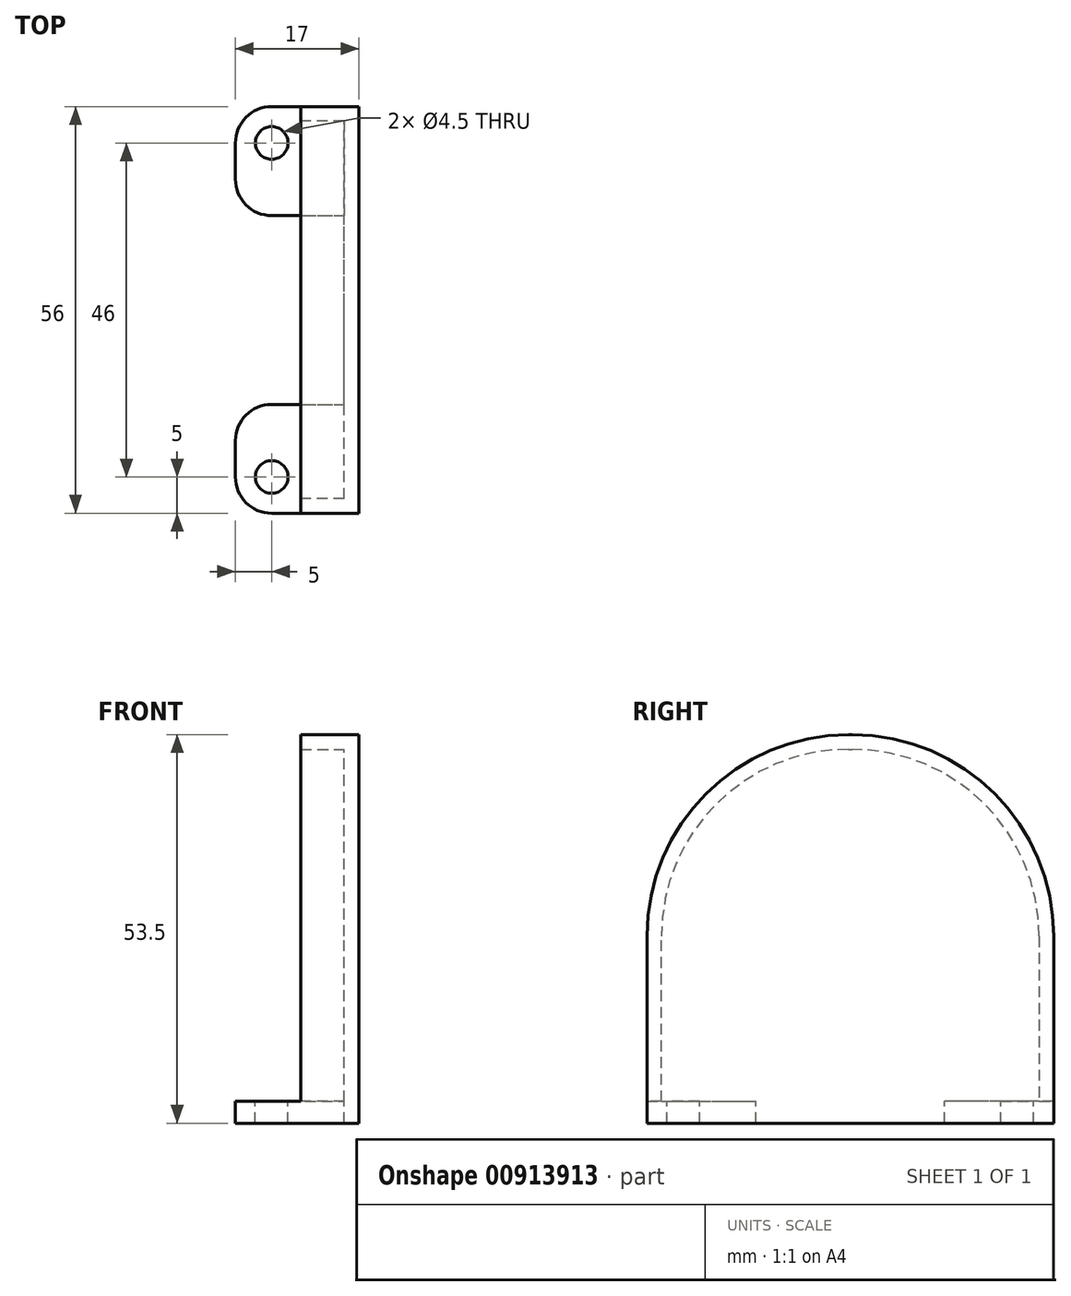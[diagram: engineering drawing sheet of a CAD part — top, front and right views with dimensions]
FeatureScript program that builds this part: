
annotation { "Feature Type Name" : "Feature", "Feature Type Description" : "" }
export const myFeature = defineFeature(function(context is Context, id is Id, definition is map)
    precondition{}
    {
        {
            var Q0;
            Q0=qCreatedBy(makeId("Right.planeOp"),FACE);
            var sketch = newSketch(context, id + "F0", { "sketchPlane" : qUnion([Q0])});
            skLineSegment(sketch, "E0.bottom", {"start": v(-28, 0) * mm, "end": v(28, 0) * mm});
            skLineSegment(sketch, "E0.top", {"start": v(-0.25, 53.5) * mm, "end": v(0.25, 53.5) * mm});
            skLineSegment(sketch, "E0.left", {"start": v(-28, 0) * mm, "end": v(-28, 25.75) * mm});
            skLineSegment(sketch, "E0.right", {"start": v(28, 0) * mm, "end": v(28, 25.75) * mm});
            skPoint(sketch, "E1.visualSharp", {"position": v(-28, 53.5) * mm});
            skArc(sketch, "E1.filletArc", {"start": v(-0.25, 53.5) * mm, "mid": v(-19.87, 45.37) * mm, "end": v(-28, 25.75) * mm});
            skPoint(sketch, "E2.visualSharp", {"position": v(28, 53.5) * mm});
            skArc(sketch, "E2.filletArc", {"start": v(28, 25.75) * mm, "mid": v(19.87, 45.37) * mm, "end": v(0.25, 53.5) * mm});
            skLineSegment(sketch, "E3", {"start": v(-28, 25.75) * mm, "end": v(28, 25.75) * mm, "construction": true});
            skSolve(sketch);
        }
        {
            var Q0;
            Q0=qSketchRegion(id+"F0",true);
            extrude(context, id + "F1", {"entities" : qUnion([Q0]), "depth" : 2 * mm, "offsetDistance" : 25 * mm});
        }
        {
            var Q0;
            Q0=makeQuery(id+"F1.opExtrude","CAP_FACE",FACE,{"disambiguationData":[OSD([sQuery(id+"F0.wireOp",EDGE,"E0.bottom"),sQuery(id+"F0.wireOp",EDGE,"E0.top"),sQuery(id+"F0.wireOp",EDGE,"E0.left"),sQuery(id+"F0.wireOp",EDGE,"E0.right"),sQuery(id+"F0.wireOp",EDGE,"E1.filletArc"),sQuery(id+"F0.wireOp",EDGE,"E2.filletArc"),sQuery(id+"F0.wireOp",EDGE,"wrzfFsvl-UCqs-aezh-ijM7-L5YhXrz3E0mf"),sQuery(id+"F0.wireOp",EDGE,"b7c118de-4fc0-4959-914e-51f86bd052230.MirrorC"),sQuery(id+"F0.wireOp",EDGE,"14c775e2-4603-4bff-89f2-d9301d5ced190.MirrorC"),sQuery(id+"F0.wireOp",EDGE,"2ef91e9a-52c1-4320-9fba-dc354453fdb00.MirrorC")])],"isStart":true});
            var sketch = newSketch(context, id + "F2", { "sketchPlane" : qUnion([Q0])});
            skArc(sketch, "E4.0", {"start": v(26, 25.75) * mm, "mid": v(18.46, 43.96) * mm, "end": v(0.25, 51.5) * mm});
            skArc(sketch, "E4.1", {"start": v(-0.25, 51.5) * mm, "mid": v(-18.46, 43.96) * mm, "end": v(-26, 25.75) * mm});
            skLineSegment(sketch, "E4.2", {"start": v(-26, 25.75) * mm, "end": v(-26, 0) * mm});
            skLineSegment(sketch, "E4.3", {"start": v(0.25, 51.5) * mm, "end": v(-0.25, 51.5) * mm});
            skLineSegment(sketch, "E4.5", {"start": v(26, 0) * mm, "end": v(26, 25.75) * mm});
            skArc(sketch, "E5.0", {"start": v(28, 25.75) * mm, "mid": v(19.87, 45.37) * mm, "end": v(0.25, 53.5) * mm});
            skArc(sketch, "E5.1", {"start": v(-0.25, 53.5) * mm, "mid": v(-19.87, 45.37) * mm, "end": v(-28, 25.75) * mm});
            skLineSegment(sketch, "E5.2", {"start": v(-28, 25.75) * mm, "end": v(-28, 0) * mm});
            skLineSegment(sketch, "E5.3", {"start": v(0.25, 53.5) * mm, "end": v(-0.25, 53.5) * mm});
            skLineSegment(sketch, "E5.4", {"start": v(-28, 0) * mm, "end": v(-26, 0) * mm});
            skLineSegment(sketch, "E5.5", {"start": v(28, 0) * mm, "end": v(28, 25.75) * mm});
            skLineSegment(sketch, "E6.trimOffspring", {"start": v(26, 0) * mm, "end": v(28, 0) * mm});
            skSolve(sketch);
        }
        {
            var Q0;
            Q0=qSketchRegion(id+"F2",true);
            extrude(context, id + "F3", {"entities" : qUnion([Q0]), "operationType" : NewBodyOperationType.ADD, "depth" : 6 * mm, "offsetDistance" : 25 * mm});
        }
        {
            var Q0;
            Q0=makeQuery(id+"F1.opExtrude","CAP_FACE",FACE,{"disambiguationData":[OSD([sQuery(id+"F0.wireOp",EDGE,"E0.bottom"),sQuery(id+"F0.wireOp",EDGE,"E0.top"),sQuery(id+"F0.wireOp",EDGE,"E0.left"),sQuery(id+"F0.wireOp",EDGE,"E0.right"),sQuery(id+"F0.wireOp",EDGE,"E1.filletArc"),sQuery(id+"F0.wireOp",EDGE,"E2.filletArc")])],"isStart":true});
            var sketch = newSketch(context, id + "F4", { "sketchPlane" : qUnion([Q0])});
            skLineSegment(sketch, "E7.bottom", {"start": v(-28, 0) * mm, "end": v(-13, 0) * mm});
            skLineSegment(sketch, "E7.top", {"start": v(-28, 3) * mm, "end": v(-13, 3) * mm});
            skLineSegment(sketch, "E7.left", {"start": v(-28, 0) * mm, "end": v(-28, 3) * mm});
            skLineSegment(sketch, "E7.right", {"start": v(-13, 0) * mm, "end": v(-13, 3) * mm});
            skLineSegment(sketch, "E8.MirrorCS", {"start": v(28, 0) * mm, "end": v(28, 3) * mm});
            skLineSegment(sketch, "E9.MirrorCS", {"start": v(28, 3) * mm, "end": v(13, 3) * mm});
            skLineSegment(sketch, "E10.MirrorCS", {"start": v(13, 0) * mm, "end": v(13, 3) * mm});
            skLineSegment(sketch, "E11.MirrorCS", {"start": v(28, 0) * mm, "end": v(13, 0) * mm});
            skSolve(sketch);
        }
        {
            var Q0;
            Q0=qSketchRegion(id+"F4",true);
            extrude(context, id + "F5", {"entities" : qUnion([Q0]), "operationType" : NewBodyOperationType.ADD, "depth" : 15 * mm, "offsetDistance" : 25 * mm});
        }
        {
            var Q0;
            Q0=makeQuery(id+"F5.opExtrude","SWEPT_FACE",FACE,{"disambiguationData":[OSD([sQuery(id+"F4.wireOp",EDGE,"E7.top")])]});
            var sketch = newSketch(context, id + "F6", { "sketchPlane" : qUnion([Q0])});
            skCircle(sketch, "E12", {"center": v(-10, 23) * mm, "radius": 2.25 * mm});
            skCircle(sketch, "E13", {"center": v(-10, -23) * mm, "radius": 2.25 * mm});
            skSolve(sketch);
        }
        {
            var Q0;
            Q0=qSketchRegion(id+"F6",true);
            extrude(context, id + "F7", {"entities" : qUnion([Q0]), "operationType" : NewBodyOperationType.REMOVE, "endBound" : BoundingType.THROUGH_ALL, "oppositeDirection" : true, "depth" : 25 * mm, "offsetDistance" : 25 * mm});
        }
        {
            var Q0;
            Q0=makeQuery(id+"F5.opExtrude","CAP_EDGE",EDGE,{"disambiguationData":[OSD([sQuery(id+"F4.wireOp",EDGE,"E7.left")])],"isStart":false});
            var Q1;
            Q1=makeQuery(id+"F5.opExtrude","CAP_EDGE",EDGE,{"disambiguationData":[OSD([sQuery(id+"F4.wireOp",EDGE,"E7.right")])],"isStart":false});
            var Q2;
            Q2=makeQuery(id+"F5.opExtrude","CAP_EDGE",EDGE,{"disambiguationData":[OSD([sQuery(id+"F4.wireOp",EDGE,"E10.MirrorCS")])],"isStart":false});
            var Q3;
            Q3=makeQuery(id+"F5.opExtrude","CAP_EDGE",EDGE,{"disambiguationData":[OSD([sQuery(id+"F4.wireOp",EDGE,"E8.MirrorCS")])],"isStart":false});
            fillet(context, id + "F8", {"entities" : qUnion([Q0, Q1, Q2, Q3]), "radius" : 5 * mm, "tangentPropagation" : true, "allowEdgeOverflow" : false});
        }
    });
